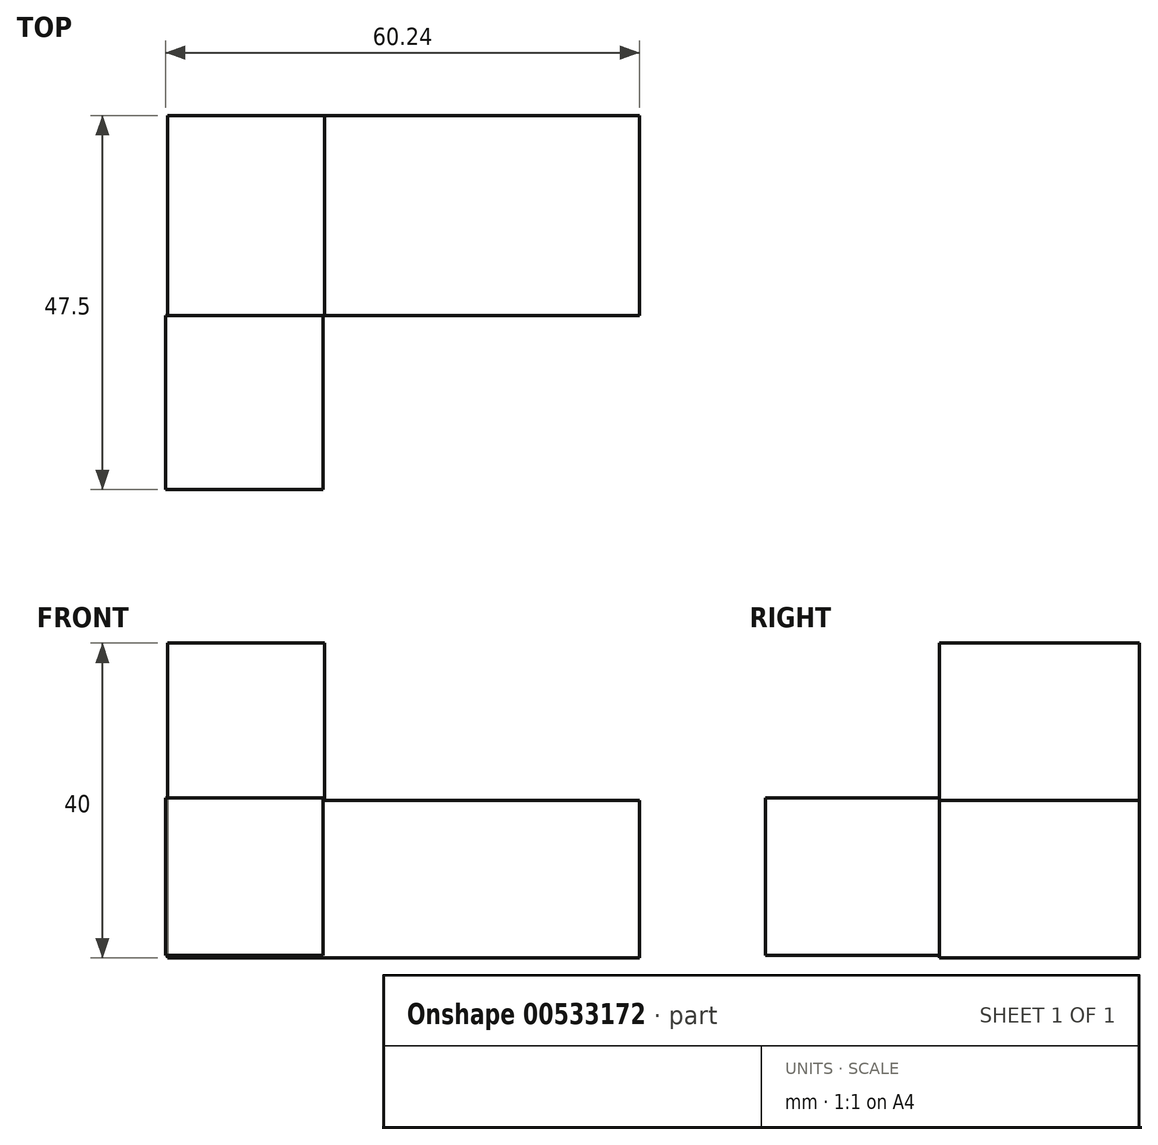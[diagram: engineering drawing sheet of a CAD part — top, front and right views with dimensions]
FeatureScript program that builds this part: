
annotation { "Feature Type Name" : "Feature", "Feature Type Description" : "" }
export const myFeature = defineFeature(function(context is Context, id is Id, definition is map)
    precondition{}
    {
        {
            var Q0;
            Q0=qCreatedBy(makeId("Front.planeOp"),FACE);
            var sketch = newSketch(context, id + "F0", { "sketchPlane" : qUnion([Q0])});
            skLineSegment(sketch, "E0.bottom", {"start": v(-37.04, 16.4) * mm, "end": v(-17.04, 16.4) * mm});
            skLineSegment(sketch, "E0.top", {"start": v(-37.04, -23.6) * mm, "end": v(-17.04, -23.6) * mm});
            skLineSegment(sketch, "E0.left", {"start": v(-37.04, 16.4) * mm, "end": v(-37.04, -23.6) * mm});
            skLineSegment(sketch, "E0.right", {"start": v(-17.04, 16.4) * mm, "end": v(-17.04, -23.6) * mm});
            skLineSegment(sketch, "E1.bottom", {"start": v(-17.04, -3.6) * mm, "end": v(22.96, -3.6) * mm});
            skLineSegment(sketch, "E1.top", {"start": v(-17.04, -23.6) * mm, "end": v(22.96, -23.6) * mm});
            skLineSegment(sketch, "E1.left", {"start": v(-17.04, -3.6) * mm, "end": v(-17.04, -23.6) * mm});
            skLineSegment(sketch, "E1.right", {"start": v(22.96, -3.6) * mm, "end": v(22.96, -23.6) * mm});
            skLineSegment(sketch, "E2.bottom", {"start": v(-37.04, -3.6) * mm, "end": v(-17.04, -3.6) * mm});
            skLineSegment(sketch, "E2.left", {"start": v(-37.04, -3.6) * mm, "end": v(-37.04, -23.6) * mm});
            skSolve(sketch);
        }
        {
            var Q0;
            Q0 = qSketchRegion(id + "F0", true);
            extrude(context, id + "F1", {"entities" : qUnion([Q0]), "oppositeDirection" : true, "depth" : 25.4 * mm, "offsetDistance" : 25.4 * mm});
        }
        {
            var Q0;
            Q0=qCreatedBy(makeId("Front.planeOp"),FACE);
            var sketch = newSketch(context, id + "F2", { "sketchPlane" : qUnion([Q0])});
            skLineSegment(sketch, "E3.bottom", {"start": v(-17.28, -3.29) * mm, "end": v(-37.28, -3.29) * mm});
            skLineSegment(sketch, "E3.top", {"start": v(-17.28, -23.29) * mm, "end": v(-37.28, -23.29) * mm});
            skLineSegment(sketch, "E3.left", {"start": v(-17.28, -3.29) * mm, "end": v(-17.28, -23.29) * mm});
            skLineSegment(sketch, "E3.right", {"start": v(-37.28, -3.29) * mm, "end": v(-37.28, -23.29) * mm});
            skSolve(sketch);
        }
        {
            var Q0;
            Q0 = qSketchRegion(id + "F2", true);
            extrude(context, id + "F3", {"entities" : qUnion([Q0]), "operationType" : NewBodyOperationType.ADD, "depth" : 22.1 * mm, "offsetDistance" : 25.4 * mm});
        }
    });
